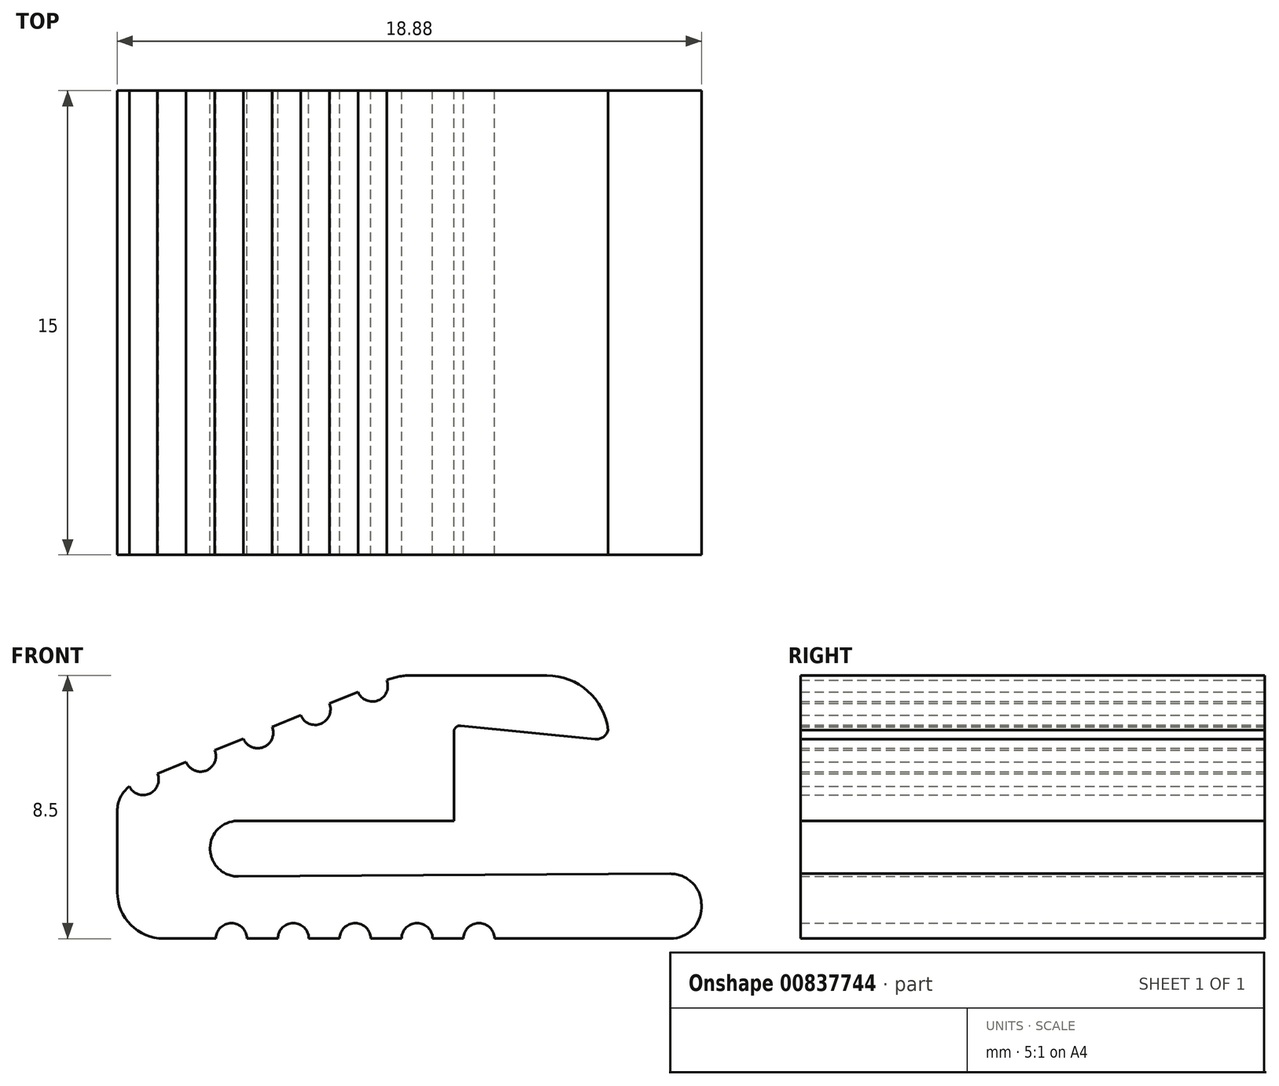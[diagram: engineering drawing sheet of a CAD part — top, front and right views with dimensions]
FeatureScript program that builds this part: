
annotation { "Feature Type Name" : "Feature", "Feature Type Description" : "" }
export const myFeature = defineFeature(function(context is Context, id is Id, definition is map)
    precondition{}
    {
        {
            var Q0;
            Q0=qCreatedBy(makeId("Front.planeOp"),FACE);
            var sketch = newSketch(context, id + "F0", { "sketchPlane" : qUnion([Q0])});
            skLineSegment(sketch, "E0", {"start": v(-42.4, 32.87) * mm, "end": v(-42.4, 32.75) * mm});
            skLineSegment(sketch, "E1", {"start": v(-40.9, 31.37) * mm, "end": v(-39.2, 31.37) * mm});
            skLineSegment(sketch, "E2", {"start": v(-23.52, 32.37) * mm, "end": v(-23.52, 32.47) * mm});
            skLineSegment(sketch, "E3", {"start": v(-24.53, 33.47) * mm, "end": v(-38.5, 33.38) * mm});
            skLineSegment(sketch, "E4", {"start": v(-39.4, 34.28) * mm, "end": v(-39.4, 34.3) * mm});
            skLineSegment(sketch, "E5", {"start": v(-38.52, 35.17) * mm, "end": v(-31.52, 35.17) * mm});
            skLineSegment(sketch, "E6", {"start": v(-31.52, 35.17) * mm, "end": v(-31.52, 38.05) * mm});
            skLineSegment(sketch, "E7", {"start": v(-31.3, 38.25) * mm, "end": v(-26.96, 37.82) * mm});
            skLineSegment(sketch, "E8", {"start": v(-26.52, 37.87) * mm, "end": v(-26.52, 38.22) * mm});
            skPoint(sketch, "E9.visualSharp", {"position": v(-26.52, 37.77) * mm});
            skArc(sketch, "E9.filletArc", {"start": v(-26.96, 37.82) * mm, "mid": v(-26.65, 37.92) * mm, "end": v(-26.52, 38.22) * mm});
            skPoint(sketch, "E10.visualSharp", {"position": v(-26.52, 39.87) * mm});
            skPoint(sketch, "E11.visualSharp", {"position": v(-23.52, 33.47) * mm});
            skArc(sketch, "E11.filletArc", {"start": v(-23.52, 32.47) * mm, "mid": v(-23.82, 33.18) * mm, "end": v(-24.53, 33.47) * mm});
            skPoint(sketch, "E12.visualSharp", {"position": v(-23.52, 31.37) * mm});
            skArc(sketch, "E12.filletArc", {"start": v(-24.52, 31.37) * mm, "mid": v(-23.81, 31.67) * mm, "end": v(-23.52, 32.37) * mm});
            skPoint(sketch, "E13.visualSharp", {"position": v(-39.4, 35.17) * mm});
            skArc(sketch, "E13.filletArc", {"start": v(-38.52, 35.17) * mm, "mid": v(-39.14, 34.92) * mm, "end": v(-39.4, 34.3) * mm});
            skPoint(sketch, "E14.visualSharp", {"position": v(-39.4, 33.37) * mm});
            skArc(sketch, "E14.filletArc", {"start": v(-39.4, 34.28) * mm, "mid": v(-39.13, 33.64) * mm, "end": v(-38.5, 33.38) * mm});
            skPoint(sketch, "E15.visualSharp", {"position": v(-42.4, 31.37) * mm});
            skArc(sketch, "E15.filletArc", {"start": v(-42.4, 32.87) * mm, "mid": v(-41.96, 31.81) * mm, "end": v(-40.9, 31.37) * mm});
            skPoint(sketch, "E16.visualSharp", {"position": v(-31.52, 38.27) * mm});
            skArc(sketch, "E16.filletArc", {"start": v(-31.3, 38.25) * mm, "mid": v(-31.45, 38.2) * mm, "end": v(-31.52, 38.05) * mm});
            skArc(sketch, "E17", {"start": v(-38.2, 31.37) * mm, "mid": v(-38.7, 31.87) * mm, "end": v(-39.2, 31.37) * mm});
            skArc(sketch, "E18", {"start": v(-36.2, 31.37) * mm, "mid": v(-36.7, 31.87) * mm, "end": v(-37.2, 31.37) * mm});
            skArc(sketch, "E19", {"start": v(-34.2, 31.37) * mm, "mid": v(-34.7, 31.87) * mm, "end": v(-35.2, 31.37) * mm});
            skArc(sketch, "E20", {"start": v(-32.2, 31.37) * mm, "mid": v(-32.7, 31.87) * mm, "end": v(-33.2, 31.37) * mm});
            skArc(sketch, "E21", {"start": v(-30.2, 31.37) * mm, "mid": v(-30.7, 31.87) * mm, "end": v(-31.2, 31.37) * mm});
            skLineSegment(sketch, "E22.trimOffspring", {"start": v(-38.2, 31.37) * mm, "end": v(-37.2, 31.37) * mm});
            skLineSegment(sketch, "E23.trimOffspring", {"start": v(-36.2, 31.37) * mm, "end": v(-35.2, 31.37) * mm});
            skLineSegment(sketch, "E24.trimOffspring", {"start": v(-34.2, 31.37) * mm, "end": v(-33.2, 31.37) * mm});
            skLineSegment(sketch, "E25.trimOffspring", {"start": v(-32.2, 31.37) * mm, "end": v(-31.2, 31.37) * mm});
            skLineSegment(sketch, "E26.trimOffspring", {"start": v(-30.2, 31.37) * mm, "end": v(-24.52, 31.37) * mm});
            skLineSegment(sketch, "E27", {"start": v(-33.68, 39.73) * mm, "end": v(-33.7, 39.72) * mm});
            skLineSegment(sketch, "E28", {"start": v(-42.4, 35.5) * mm, "end": v(-42.4, 32.87) * mm});
            skLineSegment(sketch, "E29", {"start": v(-28.52, 39.87) * mm, "end": v(-32.93, 39.87) * mm});
            skArc(sketch, "E30", {"start": v(-42.01, 36.29) * mm, "mid": v(-41.36, 36.05) * mm, "end": v(-41.1, 36.7) * mm});
            skArc(sketch, "E31", {"start": v(-40.17, 37.08) * mm, "mid": v(-39.52, 36.8) * mm, "end": v(-39.25, 37.46) * mm});
            skArc(sketch, "E32", {"start": v(-38.32, 37.83) * mm, "mid": v(-37.67, 37.56) * mm, "end": v(-37.4, 38.21) * mm});
            skArc(sketch, "E33", {"start": v(-36.47, 38.59) * mm, "mid": v(-35.82, 38.31) * mm, "end": v(-35.54, 38.97) * mm});
            skArc(sketch, "E34", {"start": v(-34.62, 39.34) * mm, "mid": v(-33.97, 39.07) * mm, "end": v(-33.7, 39.72) * mm});
            skPoint(sketch, "E35.visualSharp", {"position": v(-42.4, 36.17) * mm});
            skArc(sketch, "E35.filletArc", {"start": v(-42.01, 36.29) * mm, "mid": v(-42.3, 35.94) * mm, "end": v(-42.4, 35.5) * mm});
            skLineSegment(sketch, "E36.trimOffspring", {"start": v(-40.17, 37.08) * mm, "end": v(-41.1, 36.7) * mm});
            skLineSegment(sketch, "E37.trimOffspring", {"start": v(-38.32, 37.83) * mm, "end": v(-39.25, 37.46) * mm});
            skLineSegment(sketch, "E38.trimOffspring", {"start": v(-36.47, 38.59) * mm, "end": v(-37.4, 38.21) * mm});
            skLineSegment(sketch, "E39.trimOffspring", {"start": v(-34.62, 39.34) * mm, "end": v(-35.54, 38.97) * mm});
            skPoint(sketch, "E40.visualSharp", {"position": v(-33.32, 39.87) * mm});
            skArc(sketch, "E40.filletArc", {"start": v(-32.93, 39.87) * mm, "mid": v(-33.31, 39.84) * mm, "end": v(-33.68, 39.73) * mm});
            skArc(sketch, "E41.filletArc", {"start": v(-26.52, 37.87) * mm, "mid": v(-27.1, 39.29) * mm, "end": v(-28.52, 39.87) * mm});
            skSolve(sketch);
        }
        {
            var Q0;
            Q0=makeQuery(id+"F0.imprint","IMPRINT",FACE,{"disambiguationData":[TD([[makeQuery(id+"F0.imprint","IMPRINT",EDGE,{"derivedFrom":sQuery(id+"F0.wireOp",EDGE,"E1")}),1.0]])]});
            extrude(context, id + "F1", {"entities" : qUnion([Q0]), "depth" : 15 * mm, "offsetDistance" : 25 * mm});
        }
    });
